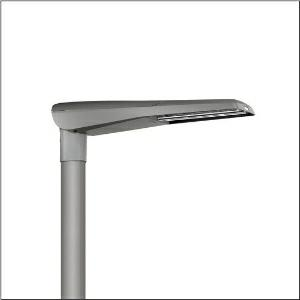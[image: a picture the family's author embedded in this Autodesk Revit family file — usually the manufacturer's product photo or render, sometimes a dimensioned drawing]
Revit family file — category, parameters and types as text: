
# Revit family: streetlight_sl_11_iq_mini___st1_2a_5xc2ac1g08he_29a3
name_source: partatom
category: Lighting Fixtures
units: mm (PartAtom-declared; Revit-internal decimal feet)

## family parameters
Cut with Voids When Loaded = No
Host = Face
Light Source = No
Part Type = Normal
Room Calculation Point = No
Round Connector Dimension = Use Diameter
Shared = No

## types (1)
- --- (1 x LED, 6820 lm, 63.6 W, 2200K)
    Apparent Load = 64 VA
    CIE Flux Codes = 32 70 96 100 100
    Color Rendering = 70
    Color Temperature = 2200K
    Default Elevation = 1800 mm
    Description = Streetlight SL 11 iQ mini, mast luminaire, primary light control with 3 zone facetted reflector, of plastic, silver coated, highly specular, primary optical cover: cover, of PMMA, transparent, light distribution: ST1.2a, light emission: direct distribution, primary light characteristic: asymmetric, installation type: post-top, side-entry, lamps: LED, High Power LED, rated values: 8.330lm | 62,2W | 133,9lm/W (begin service life); end service life: 8.330lm | 65,6W; at 50% lumin. flux: 4.165lm | 29,4W | 141,7lm/W, colour temperature: 2200/2700/3000/4000K, colour rendering: CRI > 70, light colour: 722/727/730/740, light setting 1 begin service life: 100% | 8.330lm | 62,2W | 133,9lm/W | 3.000K, light setting 1 end service life: 65,6W, further light settings possible, control: pre-setting: linear dimming characteristic, Street-Remote, Auto-Match, Temp-Guard, Lumen-Switch, Night-Set, Smart-Wire, Light-Fading, Desk-Remote (wireless, voltage-free reading and setting of iQ features in the workshop via application-optimized NFC function/RFID function), optimised constant luminous flux control (CLO 2.0), with cable H07RN-F 5x 1.5mm², mains connection: 230..240V, AC, 50/60Hz, connection cable pre-assembled, cable length: 8,5m, luminaire housing, of diecast aluminium, powder-coated, SITECO metallic grey (DB 702S), please order mast flange separately, inclination adjustable without tools: 0°, 5°, 10°, 15° (post-top) | 0°, -5°, -10°, -15° (side-entry), sealing non-destructively replaceable, multi-level sealing system, length: 736mm, width: 174mm, height: 116mm, mast flange for spigot size: 42mm (side-entry): 5XC10008XM4, 60/48mm (side-entry/post-top): 5XC10108XM2, 76/60mm (side-entry/post-top): 5XC10108XM1, equipment: Power, protection rating (complete): IP66, insulation class (complete): insulation class II (safety insulation), certification: CE, ENEC, ENEC+, VDE, impact resistance: IK10, permissible operating ambient temperature for outdoor applications: -25..+50°C, standard-compliant lighting for roads and squares, Environmental Product Declaration (EPD) tested and certified by an independent institute, packaging unit: 1 piece

Light Distribution: ST1.2a
    Height = 116 mm
    Lamp = 1 x LED
    Lamp Light Flux = 6820 lm
    Lamp Power = 63.6 W
    Lamp count = 1
    Length = 736 mm
    Luminous efficacy = 107 lm/W
    Manufacturer = Siteco
    ModVariant = No
    Model = 5XC2AC1G08HE
    Number of Poles = 1
    OnlyDefault = Yes
    Power Factor = 1
    Product Name = Streetlight SL 11 iQ mini | ST1.2a
    Product group = mast luminaire | pylon top
    ProductGroupID = 6100
    Protection Class = Protection class II
    Protection Degree = IP 66
    RLX_Detail_Level = 1
    RLX_Emergency_Light_Flux = 0 lm
    RLX_Emergency_Type = 0
    RLX_Emergency_Type_DB = No
    RlxData = <blob elided: 53657 chars, md5=b8a8b792>
    Socket = socket
    Standby Power = 0 W
    System Light Flux = 6820 lm
    System Power = 64 W
    Type Comments = individual setting: luminous flux: 100 % | dim-lin: 254 | 866 mA
    Type Image = l_1003508.jpg
    URL = http://relux.com
    VarID = @adj_041639
    Voltage = 0 V
    Weight = 0.00 kg
    Width = 174 mm

## geometry (parser evidence)
native form markers: Blend x4, Sweep x12
no freeform markers — native parametric forms only
